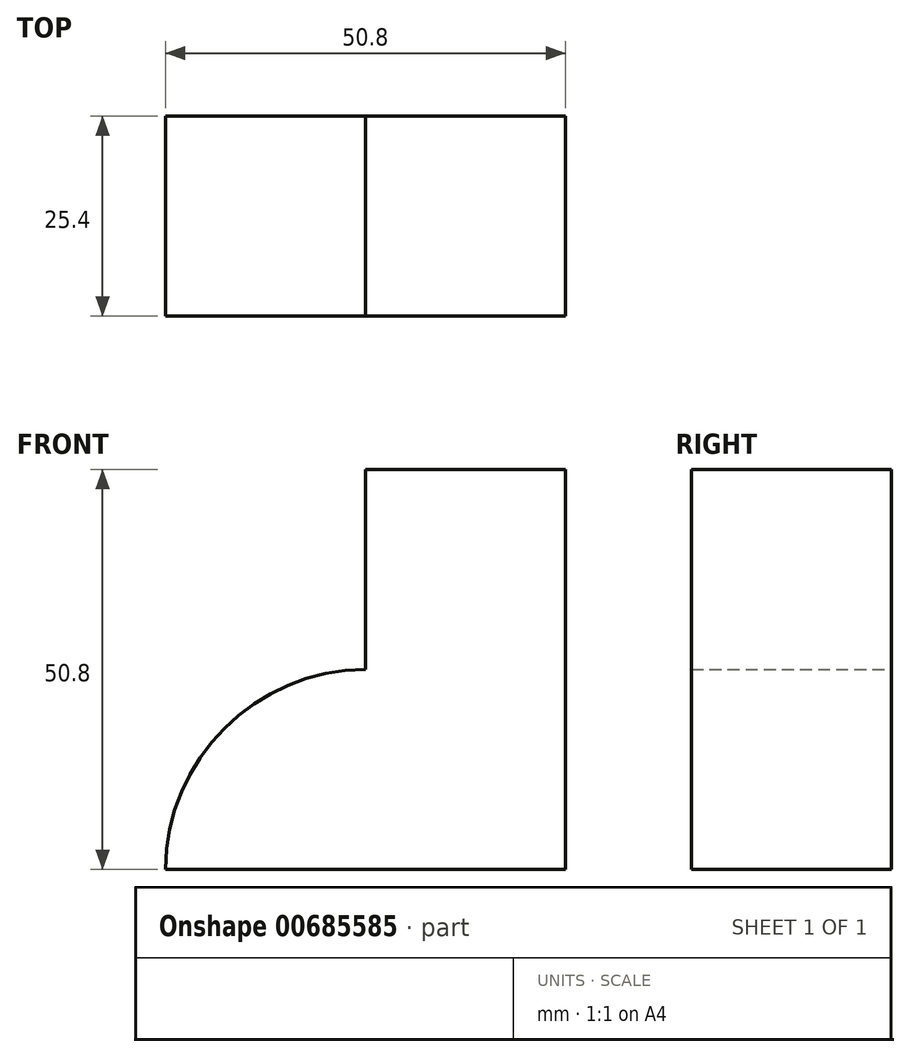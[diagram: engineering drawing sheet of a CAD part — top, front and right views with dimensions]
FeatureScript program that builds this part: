
annotation { "Feature Type Name" : "Feature", "Feature Type Description" : "" }
export const myFeature = defineFeature(function(context is Context, id is Id, definition is map)
    precondition{}
    {
        {
            var Q0;
            Q0=qCreatedBy(makeId("Front.planeOp"),FACE);
            var sketch = newSketch(context, id + "F0", { "sketchPlane" : qUnion([Q0])});
            skLineSegment(sketch, "E0", {"start": v(0, 0) * mm, "end": v(0, 50.8) * mm});
            skLineSegment(sketch, "E1", {"start": v(0, 50.8) * mm, "end": v(-25.4, 50.8) * mm});
            skLineSegment(sketch, "E2", {"start": v(-25.4, 50.8) * mm, "end": v(-25.4, 25.4) * mm});
            skLineSegment(sketch, "E3", {"start": v(0, 0) * mm, "end": v(-50.8, 0) * mm});
            skArc(sketch, "E4", {"start": v(-25.4, 25.4) * mm, "mid": v(-43.33, 17.93) * mm, "end": v(-50.8, 0) * mm});
            skSolve(sketch);
        }
        {
            var Q0;
            Q0 = qSketchRegion(id + "F0", true);
            extrude(context, id + "F1", {"entities" : qUnion([Q0]), "depth" : 25.4 * mm, "offsetDistance" : 25.4 * mm});
        }
    });
